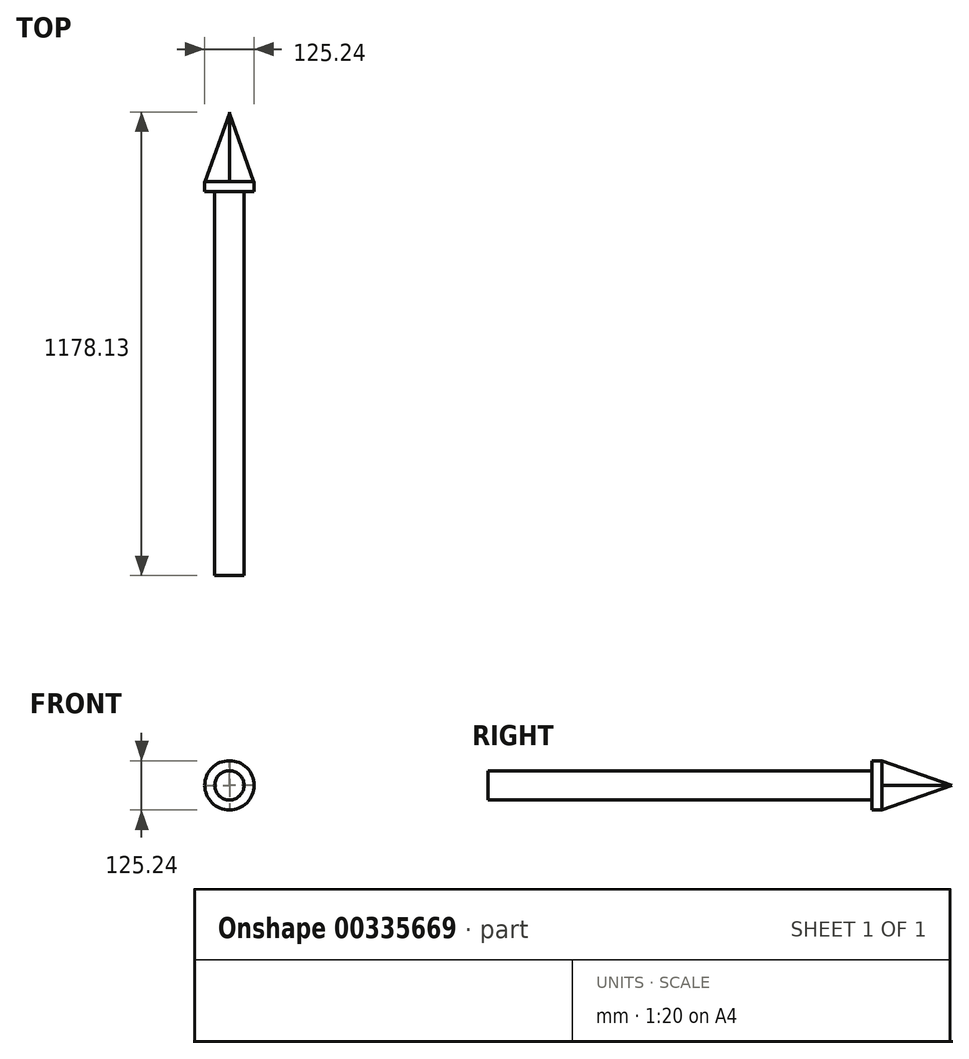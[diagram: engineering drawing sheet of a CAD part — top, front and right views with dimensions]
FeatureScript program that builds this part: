
annotation { "Feature Type Name" : "Feature", "Feature Type Description" : "" }
export const myFeature = defineFeature(function(context is Context, id is Id, definition is map)
    precondition{}
    {
        {
            var Q0;
            Q0=qCreatedBy(makeId("Front.planeOp"),FACE);
            var sketch = newSketch(context, id + "F0", { "sketchPlane" : qUnion([Q0])});
            skCircle(sketch, "E0", {"center": v(0, 0) * mm, "radius": 62.62 * mm});
            skSolve(sketch);
        }
        {
            var Q0;
            Q0=makeQuery(id+"F0.imprint","IMPRINT",FACE,{"disambiguationData":[TD([[makeQuery(id+"F0.imprint","IMPRINT",EDGE,{"derivedFrom":sQuery(id+"F0.wireOp",EDGE,"E0")}),1.0]])]});
            extrude(context, id + "F1", {"entities" : qUnion([Q0]), "depth" : 25.4 * mm});
        }
        {
            var Q0;
            Q0=qCreatedBy(makeId("Right.planeOp"),FACE);
            var sketch = newSketch(context, id + "F2", { "sketchPlane" : qUnion([Q0])});
            skLineSegment(sketch, "E1", {"start": v(0, 0) * mm, "end": v(177.37, 0) * mm});
            skLineSegment(sketch, "E2", {"start": v(177.37, 0) * mm, "end": v(0, -62.01) * mm});
            skLineSegment(sketch, "E3", {"start": v(0, -62.01) * mm, "end": v(0, 0) * mm});
            skLineSegment(sketch, "E4.MirrorCS", {"start": v(0, 62.01) * mm, "end": v(0, 0) * mm});
            skLineSegment(sketch, "E5.MirrorCS", {"start": v(177.37, 0) * mm, "end": v(0, 62.01) * mm});
            skLineSegment(sketch, "E6.1.0", {"start": v(0, 0) * mm, "end": v(-88.69, 153.6) * mm});
            skLineSegment(sketch, "E6.2.0", {"start": v(0, 0) * mm, "end": v(-88.69, -153.6) * mm});
            skPoint(sketch, "E6.center", {"position": v(0, 0) * mm});
            skSolve(sketch);
        }
        {
            var Q0;
            Q0=qCreatedBy(makeId("Top.planeOp"),FACE);
            var sketch = newSketch(context, id + "F3", { "sketchPlane" : qUnion([Q0])});
            skLineSegment(sketch, "E7", {"start": v(0, 173.34) * mm, "end": v(0, 0) * mm});
            skLineSegment(sketch, "E8", {"start": v(0, 0) * mm, "end": v(-61.59, 0) * mm});
            skLineSegment(sketch, "E9", {"start": v(-61.59, 0) * mm, "end": v(0, 173.34) * mm});
            skLineSegment(sketch, "E10", {"start": v(61.12, 0) * mm, "end": v(0, 173.34) * mm});
            skLineSegment(sketch, "E11", {"start": v(61.12, 0) * mm, "end": v(0, 0) * mm});
            skSolve(sketch);
        }
        {
            var Q0;
            Q0 = qSketchRegion(id + "F3", true);
            extrude(context, id + "F4", {"entities" : qUnion([Q0]), "operationType" : NewBodyOperationType.ADD, "endBound" : BoundingType.SYMMETRIC, "depth" : 0 * mm});
        }
        {
            var Q0;
            Q0=makeQuery(id+"F2.imprint","IMPRINT",FACE,{"disambiguationData":[TD([[makeQuery(id+"F2.imprint","IMPRINT",EDGE,{"derivedFrom":sQuery(id+"F2.wireOp",EDGE,"E1")}),1.0]])]});
            var Q1;
            Q1=makeQuery(id+"F2.imprint","IMPRINT",FACE,{"disambiguationData":[TD([[makeQuery(id+"F2.imprint","IMPRINT",EDGE,{"derivedFrom":sQuery(id+"F2.wireOp",EDGE,"E1")}),-1.0]])]});
            extrude(context, id + "F5", {"entities" : qUnion([Q0, Q1]), "operationType" : NewBodyOperationType.ADD, "endBound" : BoundingType.SYMMETRIC, "depth" : 0.25 * mm});
        }
        {
            var Q0;
            Q0=makeQuery(id+"F1.opExtrude","CAP_FACE",FACE,{"disambiguationData":[OSD([sQuery(id+"F0.wireOp",EDGE,"E0")])],"isStart":false});
            var sketch = newSketch(context, id + "F6", { "sketchPlane" : qUnion([Q0])});
            skCircle(sketch, "E12", {"center": v(0, 0) * mm, "radius": 37.22 * mm});
            skSolve(sketch);
        }
        {
            var Q0;
            Q0=makeQuery(id+"F6.imprint","IMPRINT",FACE,{"disambiguationData":[TD([[makeQuery(id+"F6.imprint","IMPRINT",EDGE,{"derivedFrom":sQuery(id+"F6.wireOp",EDGE,"E12")}),1.0]])]});
            extrude(context, id + "F7", {"entities" : qUnion([Q0]), "operationType" : NewBodyOperationType.ADD, "depth" : 975.36 * mm});
        }
    });
